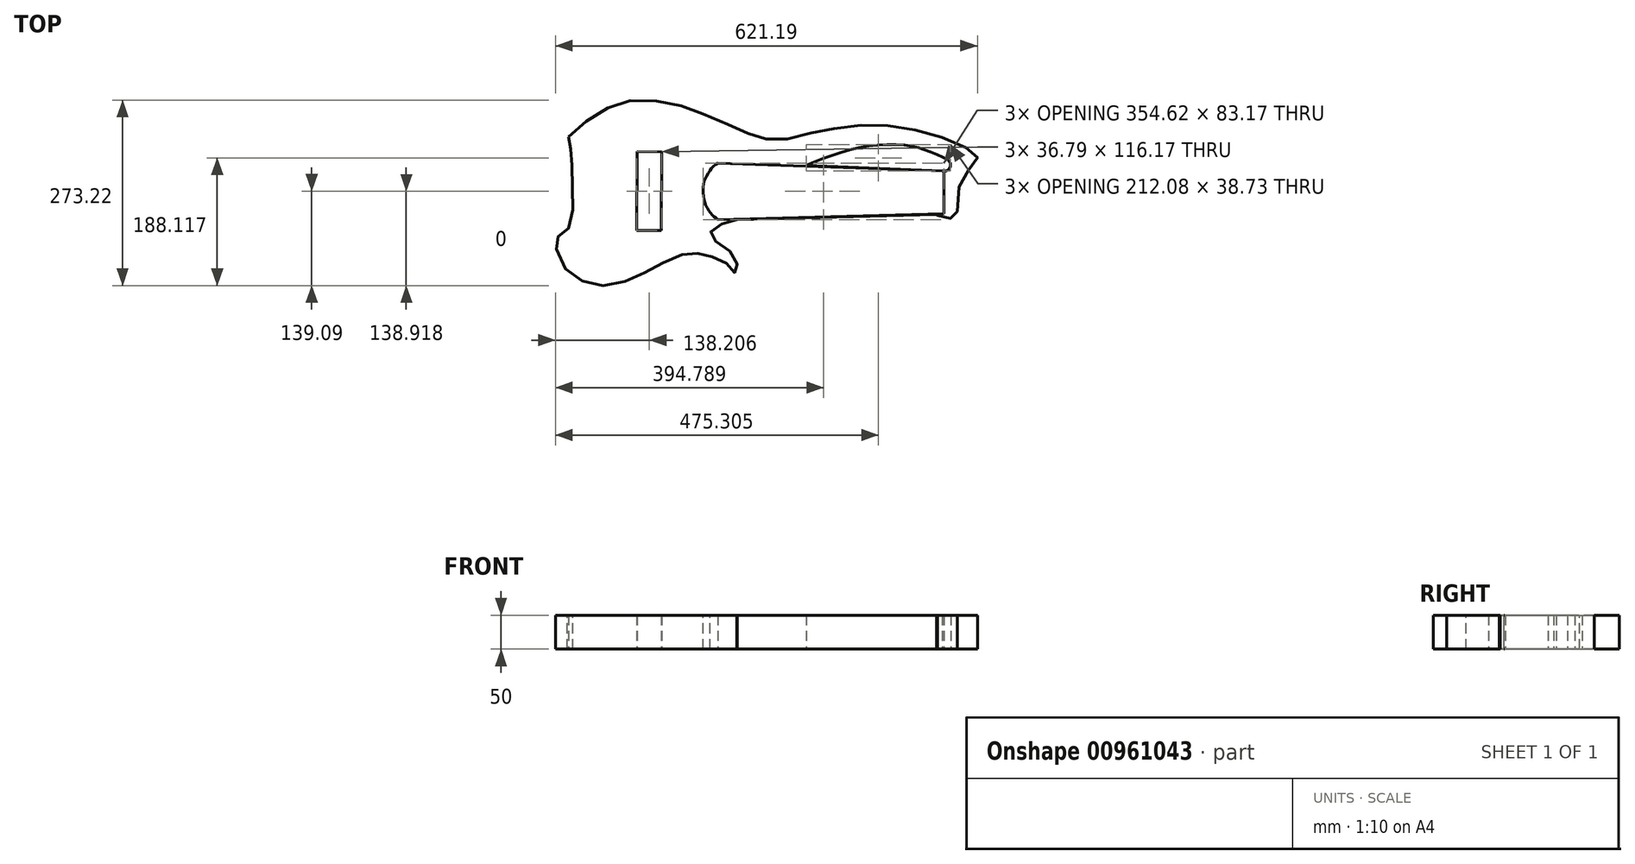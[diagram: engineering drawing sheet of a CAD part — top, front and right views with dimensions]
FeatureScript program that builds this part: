
annotation { "Feature Type Name" : "Feature", "Feature Type Description" : "" }
export const myFeature = defineFeature(function(context is Context, id is Id, definition is map)
    precondition{}
    {
        {
            var Q0;
            Q0=qCreatedBy(makeId("Top.planeOp"),FACE);
            var sketch = newSketch(context, id + "F0", { "sketchPlane" : qUnion([Q0])});
            skPoint(sketch, "E0.middle", {"position": v(0, 0) * mm});
            skFitSpline(sketch, "E1", {"points": [v(-239.8, 82.4) * mm, v(-213.31, 105.4) * mm, v(-178.46, 126.32) * mm, v(-145, 136.08) * mm, v(-101.77, 133.98) * mm, v(-64.82, 124.92) * mm, v(-31.36, 111.68) * mm, v(9.08, 94.25) * mm, v(30.69, 84.49) * mm, v(53.7, 78.9) * mm, v(82.97, 79.6) * mm, v(118.53, 88.67) * mm, v(153.39, 94.94) * mm, v(200.1, 99.82) * mm, v(244.71, 97.04) * mm, v(292.82, 87.27) * mm, v(336.04, 71.24) * mm, v(360.44, 56.6) * mm, v(361.83, 51.02) * mm, v(355.56, 41.96) * mm, v(340.92, 21.74) * mm, v(333.25, 0) * mm, v(332.55, -31.94) * mm, v(332.55, -32.63) * mm, v(323.5, -37.51) * mm, v(308.15, -35.42) * mm, v(303.27, -33.33) * mm], "startDerivative": vector(618.69, 612.62) * mm, "endDerivative": vector(245.75, -245.75) * mm});
            skLineSegment(sketch, "E2", {"start": v(301.87, -31.93) * mm, "end": v(7.68, -39.6) * mm});
            skFitSpline(sketch, "E3", {"points": [v(7.68, -39.6) * mm, v(-9.75, -43.79) * mm, v(-24.39, -52.15) * mm, v(-30.66, -57.73) * mm, v(-29.96, -64.7) * mm, v(-19.5, -73.77) * mm, v(-0.68, -87.01) * mm, v(8.38, -102.35) * mm, v(7.68, -111.41) * mm, v(6.99, -116.3) * mm, v(0, -116.3) * mm, v(-6.96, -104.44) * mm, v(-23.69, -96.07) * mm, v(-34.84, -91.9) * mm, v(-53.67, -88.4) * mm, v(-71.1, -90.5) * mm, v(-98.28, -101.65) * mm, v(-126.17, -116.99) * mm, v(-156.15, -130.24) * mm, v(-191.7, -136.5) * mm, v(-222.38, -128.14) * mm, v(-246.78, -108.62) * mm, v(-258.63, -78.65) * mm, v(-257.23, -66.1) * mm, v(-248.87, -60.52) * mm, v(-239.1, -52.15) * mm, v(-234.92, -46.58) * mm, v(-234.92, 55.9) * mm, v(-235.62, 62.87) * mm, v(-239.8, 69.15) * mm, v(-239.8, 82.4) * mm], "startDerivative": vector(-530.9, -85.09) * mm, "endDerivative": vector(291.54, 801.75) * mm});
            skFitSpline(sketch, "E4", {"points": [v(110.16, 40.57) * mm, v(158.27, 58.7) * mm, v(209.16, 69.85) * mm, v(257.26, 69.85) * mm, v(283.75, 63.57) * mm, v(308.15, 53.81) * mm, v(322.1, 44.75) * mm, v(322.1, 37.78) * mm, v(317.91, 32.9) * mm, v(310.24, 32.2) * mm], "startDerivative": vector(268.52, 112.98) * mm, "endDerivative": vector(-130.09, 6.83) * mm});
            skLineSegment(sketch, "E5", {"start": v(310.24, 32.2) * mm, "end": v(110.16, 40.57) * mm});
            skLineSegment(sketch, "E6", {"start": v(303.27, -33.33) * mm, "end": v(301.87, -31.93) * mm});
            skFitSpline(sketch, "E7", {"points": [v(-19.75, 43.96) * mm, v(-28.07, 37.72) * mm, v(-34.3, 28.36) * mm, v(-40.03, 17.44) * mm, v(-41.59, 6.53) * mm, v(-41.07, -5.43) * mm, v(-37.43, -18.94) * mm, v(-31.7, -28.3) * mm, v(-25.47, -35.06) * mm, v(-20.27, -39.22) * mm], "startDerivative": vector(-94.86, -60.12) * mm, "endDerivative": vector(59.6, -44.4) * mm});
            skLineSegment(sketch, "E8", {"start": v(-19.75, 43.96) * mm, "end": v(313, 32.06) * mm});
            skLineSegment(sketch, "E9", {"start": v(313, -30.58) * mm, "end": v(-20.27, -39.22) * mm});
            skLineSegment(sketch, "E10", {"start": v(313, 32.06) * mm, "end": v(313, -30.58) * mm});
            skLineSegment(sketch, "E11", {"start": v(-138.55, 60.62) * mm, "end": v(-139.29, -55.31) * mm});
            skLineSegment(sketch, "E12", {"start": v(-139.29, -55.31) * mm, "end": v(-103.24, -55.55) * mm});
            skLineSegment(sketch, "E13", {"start": v(-103.24, -55.55) * mm, "end": v(-102.5, 60.4) * mm});
            skLineSegment(sketch, "E14", {"start": v(-102.5, 60.4) * mm, "end": v(-138.55, 60.62) * mm});
            skSolve(sketch);
        }
        {
            var Q0;
            Q0 = qSketchRegion(id + "F0", true);
            extrude(context, id + "F1", {"entities" : qUnion([Q0]), "depth" : 50 * mm, "offsetDistance" : 25 * mm});
        }
    });
